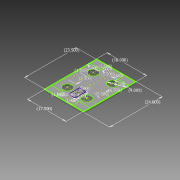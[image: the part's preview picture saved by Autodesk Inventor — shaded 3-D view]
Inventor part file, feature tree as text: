
AUTODESK INVENTOR PART (.ipt)
format: ipt  version: 2015 (Build 190159000, 159)  size: 136,192 bytes
history: native  units: in
note: dims shown in document units (in); Inventor stores cm internally (conversion verified against a paired STEP export)
features: other x3, sketch x2
ambient origin geometry x8: Origin, YZ Plane, XZ Plane, XY Plane, X Axis, Y Axis, Z Axis, Center Point
bodies: Solid1 (feature_tree)
feature tree (5):
  other  "board_with_hole_pipes.ipt"
  sketch  "Sketch2"  dims[d0=0.1969in]
  other  "Solid1::board_with_hole_pipes.ipt"
  other  "TaggingFeature1"
  sketch  "Sketch3"  dims[d1=18.0in d2=24.0in d3=23.5in d4=17.5in d5=5.5in d6=1.5in d9=5.5in d10=1.5in d11=5.5in d12=1.5in d15=4.0in d18=5.5in d19=1.5in d22=5.0in d23=3.0in d24=5.0in d25=3.0in d26=3.0in d27=3.0in d28=3.0in d29=5.0in]
